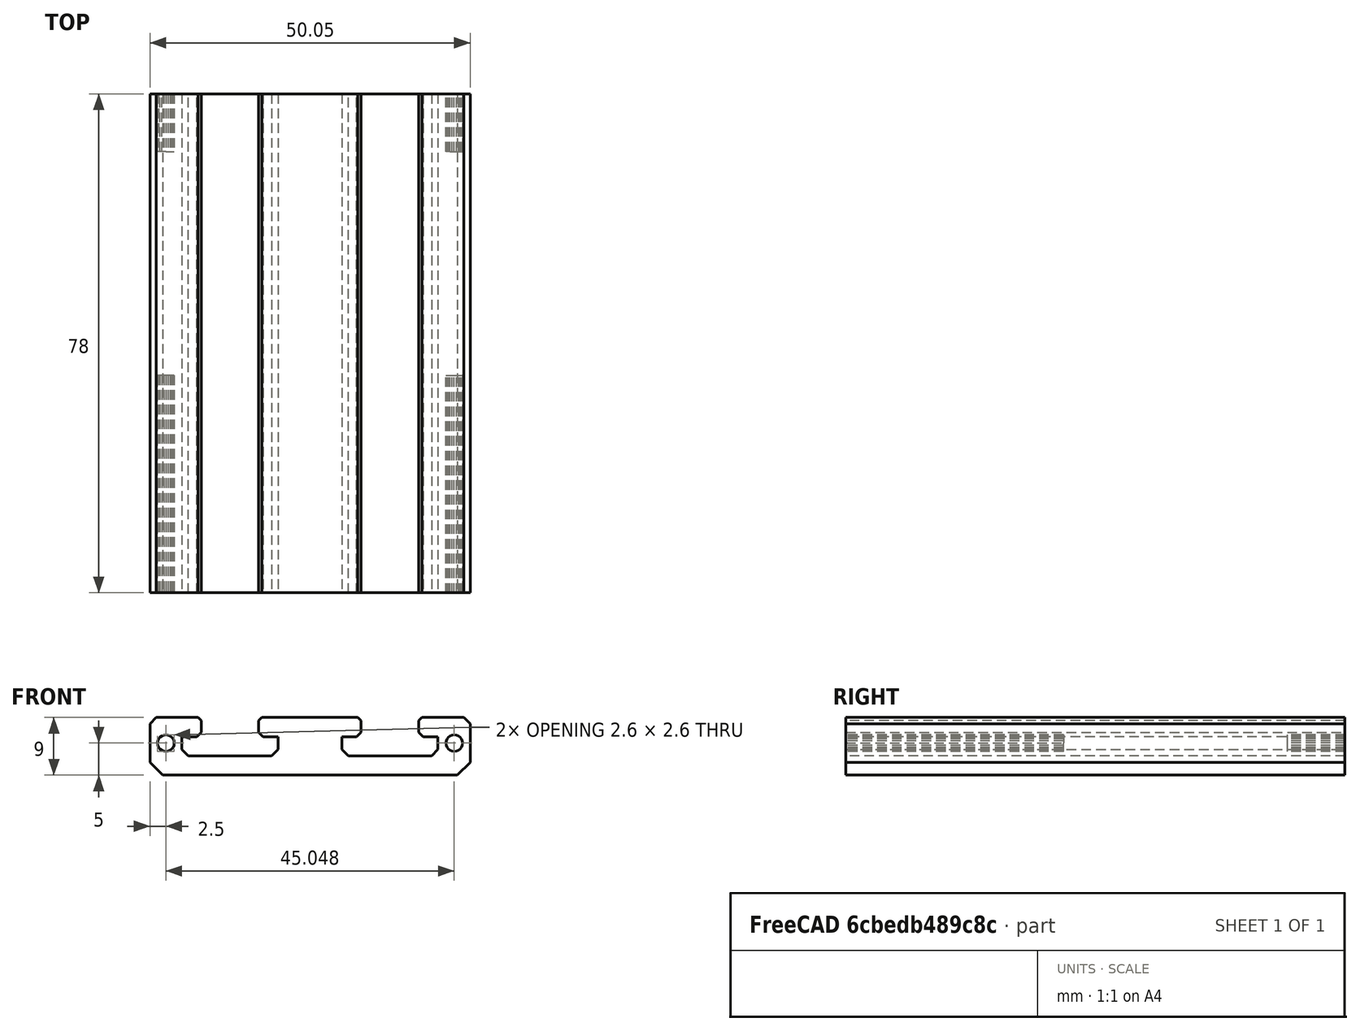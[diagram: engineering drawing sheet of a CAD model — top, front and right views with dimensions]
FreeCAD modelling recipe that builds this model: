
FCSTD DOCUMENT  (FreeCAD 0.19R24267 +148 (Git))
Label: XYstage_Rail
License: All rights reserved
LicenseURL: http://en.wikipedia.org/wiki/All_rights_reserved
objects: Part::Refine×2, Part::Feature×1, PartDesign::FeatureBase×1, PartDesign::Pad×1, PartDesign::Body×1
note: 7 computed .brp shape members not serialized (recipe doc carries the construction recipe); baked Part::Feature solids carry a one-line shape summary decoded from their .brp

FEATURE [Part::Feature] LinearRailTest_Rail_test001_solid  label="LinearRailTest_Rail_test001 (Solid)"
  shape: bbox 50.05 x 53 x 9 mm, 1080 faces (baked)
FEATURE [Part::Refine] LinearRailTest_Rail_test001_solid001  label="LinearRailTest_Rail_test001 (Solid)001"
  Source = -> LinearRailTest_Rail_test001_solid
FEATURE [PartDesign::FeatureBase] BaseFeature
  BaseFeature = -> LinearRailTest_Rail_test001_solid001
FEATURE [PartDesign::Pad] Pad
  BaseFeature = -> BaseFeature
  Direction = (1,1,1)
  Length = 25
  Length2 = 100
  Profile = -> BaseFeature [Face6]
  Type = 0
FEATURE [PartDesign::Body] Body
  BaseFeature = -> LinearRailTest_Rail_test001_solid001
  Group = -> [BaseFeature,Pad]
  Origin = -> Origin
  Tip = -> Pad
FEATURE [Part::Refine] Body001
  Source = -> Body
